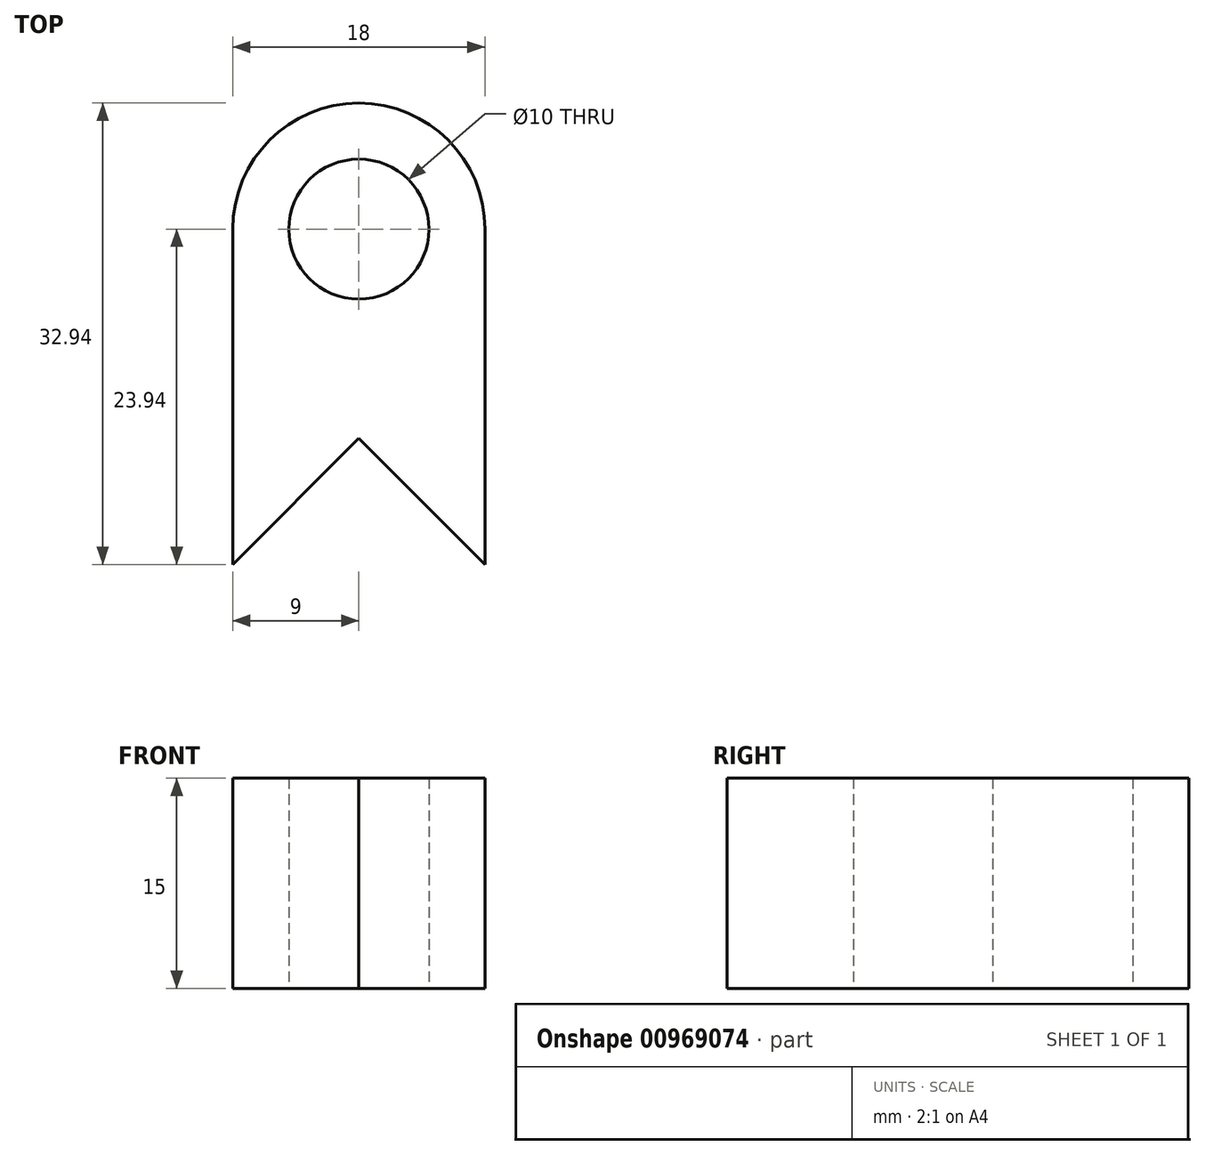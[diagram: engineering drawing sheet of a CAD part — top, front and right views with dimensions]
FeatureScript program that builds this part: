
annotation { "Feature Type Name" : "Feature", "Feature Type Description" : "" }
export const myFeature = defineFeature(function(context is Context, id is Id, definition is map)
    precondition{}
    {
        {
            var Q0;
            Q0=qCreatedBy(makeId("Top.planeOp"),FACE);
            var sketch = newSketch(context, id + "F0", { "sketchPlane" : qUnion([Q0])});
            skCircle(sketch, "E0", {"center": v(0, 0) * mm, "radius": 5 * mm});
            skArc(sketch, "E1.0", {"start": v(9, 0) * mm, "mid": v(0, 9) * mm, "end": v(-9, 0) * mm});
            skLineSegment(sketch, "E2", {"start": v(-9, 0) * mm, "end": v(-9, -23.94) * mm});
            skLineSegment(sketch, "E3", {"start": v(0, -14.94) * mm, "end": v(9, -23.94) * mm});
            skLineSegment(sketch, "E4", {"start": v(0, -14.94) * mm, "end": v(-9, -23.94) * mm});
            skLineSegment(sketch, "E5.MirrorCS", {"start": v(9, 0) * mm, "end": v(9, -23.94) * mm});
            skPoint(sketch, "E6.orphan", {"position": v(9, -27.84) * mm});
            skPoint(sketch, "E7.orphan", {"position": v(-9, -27.84) * mm});
            skSolve(sketch);
        }
        {
            var Q0;
            Q0=makeQuery(id+"F0.imprint","IMPRINT",FACE,{"disambiguationData":[TD([[makeQuery(id+"F0.imprint","IMPRINT",EDGE,{"derivedFrom":sQuery(id+"F0.wireOp",EDGE,"E0")}),-1.0]])]});
            extrude(context, id + "F1", {"entities" : qUnion([Q0]), "depth" : 15 * mm, "offsetDistance" : 25 * mm});
        }
    });
